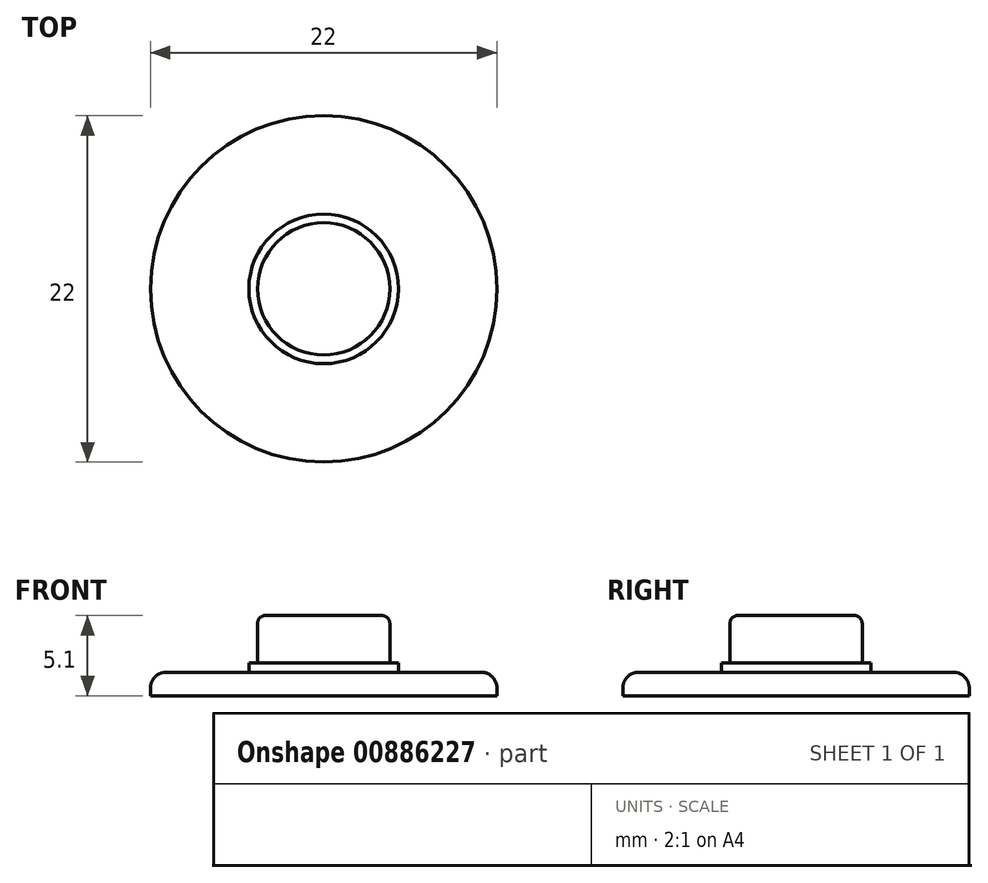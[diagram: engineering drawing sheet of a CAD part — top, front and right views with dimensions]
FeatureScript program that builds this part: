
annotation { "Feature Type Name" : "Feature", "Feature Type Description" : "" }
export const myFeature = defineFeature(function(context is Context, id is Id, definition is map)
    precondition{}
    {
        {
            var Q0;
            Q0=qCreatedBy(makeId("Top.planeOp"),FACE);
            var sketch = newSketch(context, id + "F0", { "sketchPlane" : qUnion([Q0])});
            skCircle(sketch, "E0", {"center": v(0, 0) * mm, "radius": 11 * mm});
            skCircle(sketch, "E1", {"center": v(0, 0) * mm, "radius": 4.2 * mm});
            skCircle(sketch, "E2", {"center": v(0, 0) * mm, "radius": 4.75 * mm});
            skSolve(sketch);
        }
        {
            var Q0;
            Q0=makeQuery(id+"F0.imprint","IMPRINT",FACE,{"disambiguationData":[TD([[makeQuery(id+"F0.imprint","IMPRINT",EDGE,{"derivedFrom":sQuery(id+"F0.wireOp",EDGE,"E0")}),1.0]])]});
            var Q1;
            Q1=makeQuery(id+"F0.imprint","IMPRINT",FACE,{"disambiguationData":[TD([[makeQuery(id+"F0.imprint","IMPRINT",EDGE,{"derivedFrom":sQuery(id+"F0.wireOp",EDGE,"E1")}),1.0]])]});
            var Q2;
            Q2=makeQuery(id+"F0.imprint","IMPRINT",FACE,{"disambiguationData":[TD([[makeQuery(id+"F0.imprint","IMPRINT",EDGE,{"derivedFrom":sQuery(id+"F0.wireOp",EDGE,"E1")}),-1.0]])]});
            extrude(context, id + "F1", {"entities" : qUnion([Q0, Q1, Q2]), "oppositeDirection" : true, "depth" : 1.5 * mm, "offsetDistance" : 25 * mm});
        }
        {
            var Q0;
            Q0=makeQuery(id+"F0.imprint","IMPRINT",FACE,{"disambiguationData":[TD([[makeQuery(id+"F0.imprint","IMPRINT",EDGE,{"derivedFrom":sQuery(id+"F0.wireOp",EDGE,"E1")}),1.0]])]});
            extrude(context, id + "F2", {"entities" : qUnion([Q0]), "operationType" : NewBodyOperationType.ADD, "depth" : 3.6 * mm, "offsetDistance" : 25 * mm});
        }
        {
            var Q0;
            Q0=makeQuery(id+"F1.opExtrude","CAP_EDGE",EDGE,{"disambiguationData":[OSD([sQuery(id+"F0.wireOp",EDGE,"E0")])],"isStart":true});
            fillet(context, id + "F3", {"entities" : qUnion([Q0]), "radius" : 1 * mm, "tangentPropagation" : true, "allowEdgeOverflow" : false});
        }
        {
            var Q0;
            Q0=makeQuery(id+"F2.opExtrude","CAP_EDGE",EDGE,{"disambiguationData":[OSD([sQuery(id+"F0.wireOp",EDGE,"E1")])],"isStart":false});
            fillet(context, id + "F4", {"entities" : qUnion([Q0]), "radius" : 0.5 * mm, "tangentPropagation" : true, "allowEdgeOverflow" : false});
        }
        {
            var Q0;
            Q0=makeQuery(id+"F0.imprint","IMPRINT",FACE,{"disambiguationData":[TD([[makeQuery(id+"F0.imprint","IMPRINT",EDGE,{"derivedFrom":sQuery(id+"F0.wireOp",EDGE,"E1")}),-1.0]])]});
            extrude(context, id + "F5", {"entities" : qUnion([Q0]), "operationType" : NewBodyOperationType.ADD, "depth" : 0.6 * mm, "offsetDistance" : 25 * mm});
        }
    });
